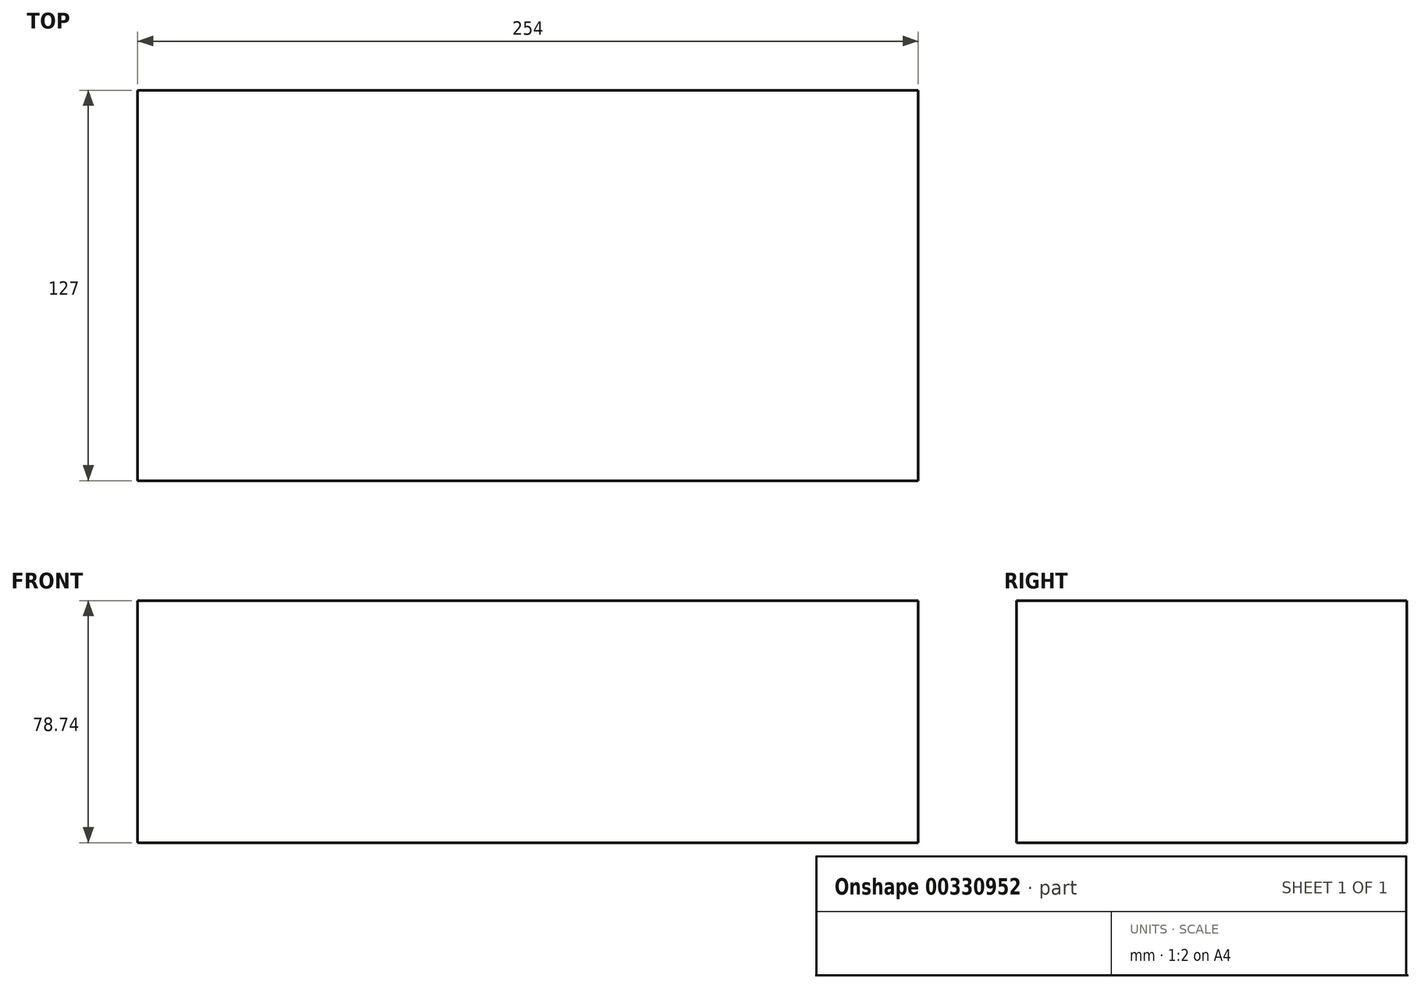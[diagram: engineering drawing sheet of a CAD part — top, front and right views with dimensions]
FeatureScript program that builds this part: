
annotation { "Feature Type Name" : "Feature", "Feature Type Description" : "" }
export const myFeature = defineFeature(function(context is Context, id is Id, definition is map)
    precondition{}
    {
        {
            var Q0;
            Q0=qCreatedBy(makeId("Top.planeOp"),FACE);
            var sketch = newSketch(context, id + "F0", { "sketchPlane" : qUnion([Q0])});
            skLineSegment(sketch, "E0.bottom", {"start": v(-143.3, 60.16) * mm, "end": v(110.7, 60.16) * mm});
            skLineSegment(sketch, "E0.top", {"start": v(-143.3, -66.84) * mm, "end": v(110.7, -66.84) * mm});
            skLineSegment(sketch, "E0.left", {"start": v(-143.3, 60.16) * mm, "end": v(-143.3, -66.84) * mm});
            skLineSegment(sketch, "E0.right", {"start": v(110.7, 60.16) * mm, "end": v(110.7, -66.84) * mm});
            skSolve(sketch);
        }
        {
            var Q0;
            Q0 = qSketchRegion(id + "F0", true);
            extrude(context, id + "F1", {"entities" : qUnion([Q0]), "depth" : 78.74 * mm});
        }
    });
